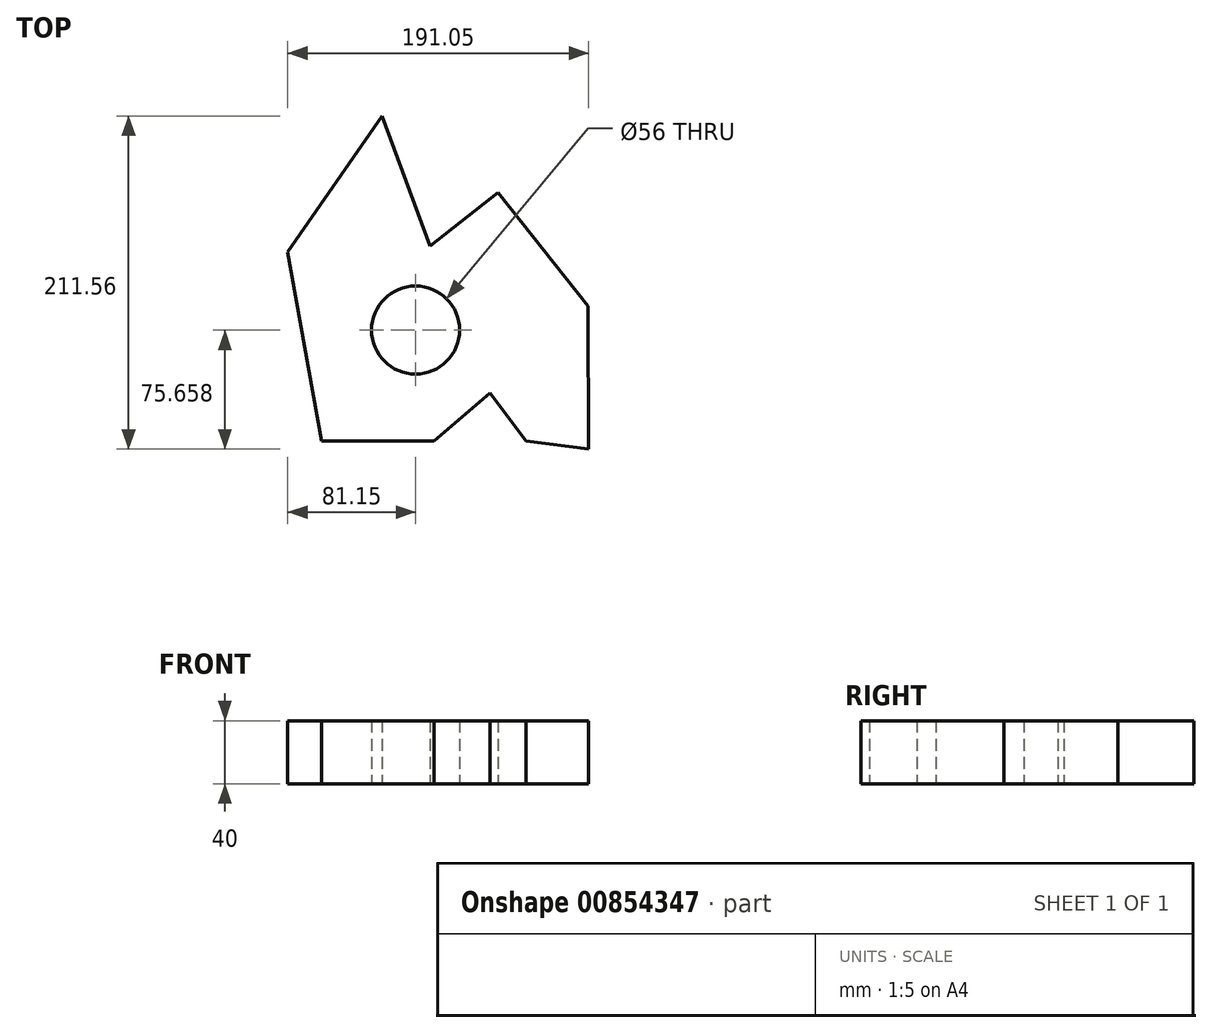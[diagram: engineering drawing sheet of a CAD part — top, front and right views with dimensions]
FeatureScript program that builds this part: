
annotation { "Feature Type Name" : "Feature", "Feature Type Description" : "" }
export const myFeature = defineFeature(function(context is Context, id is Id, definition is map)
    precondition{}
    {
        {
            var Q0;
            Q0=qCreatedBy(makeId("Top.planeOp"),FACE);
            var sketch = newSketch(context, id + "F0", { "sketchPlane" : qUnion([Q0])});
            skLineSegment(sketch, "E0", {"start": v(-21.43, 120.56) * mm, "end": v(-81.15, 34.2) * mm});
            skLineSegment(sketch, "E1", {"start": v(-21.43, 120.56) * mm, "end": v(9.15, 38.05) * mm});
            skLineSegment(sketch, "E2", {"start": v(9.15, 38.05) * mm, "end": v(52.3, 72.16) * mm});
            skLineSegment(sketch, "E3", {"start": v(52.3, 72.16) * mm, "end": v(109.36, 0) * mm});
            skLineSegment(sketch, "E4", {"start": v(109.36, 0) * mm, "end": v(109.9, -91) * mm});
            skLineSegment(sketch, "E5", {"start": v(109.9, -91) * mm, "end": v(70.25, -85.66) * mm});
            skLineSegment(sketch, "E6", {"start": v(70.25, -85.66) * mm, "end": v(47.2, -55.46) * mm});
            skLineSegment(sketch, "E7", {"start": v(47.2, -119.83) * mm, "end": v(-59.8, -119.83) * mm});
            skLineSegment(sketch, "E8", {"start": v(47.2, -55.46) * mm, "end": v(-5.77, -100.48) * mm});
            skLineSegment(sketch, "E9", {"start": v(11.65, -85.66) * mm, "end": v(-59.8, -85.66) * mm});
            skLineSegment(sketch, "E10", {"start": v(-59.8, -85.66) * mm, "end": v(-81.15, 34.2) * mm});
            skCircle(sketch, "E11", {"center": v(0, -15.34) * mm, "radius": 28 * mm});
            skSolve(sketch);
        }
        {
            var Q0;
            Q0=qSketchRegion(id+"F0",true);
            extrude(context, id + "F1", {"entities" : qUnion([Q0]), "depth" : 40 * mm, "offsetDistance" : 25 * mm});
        }
    });
